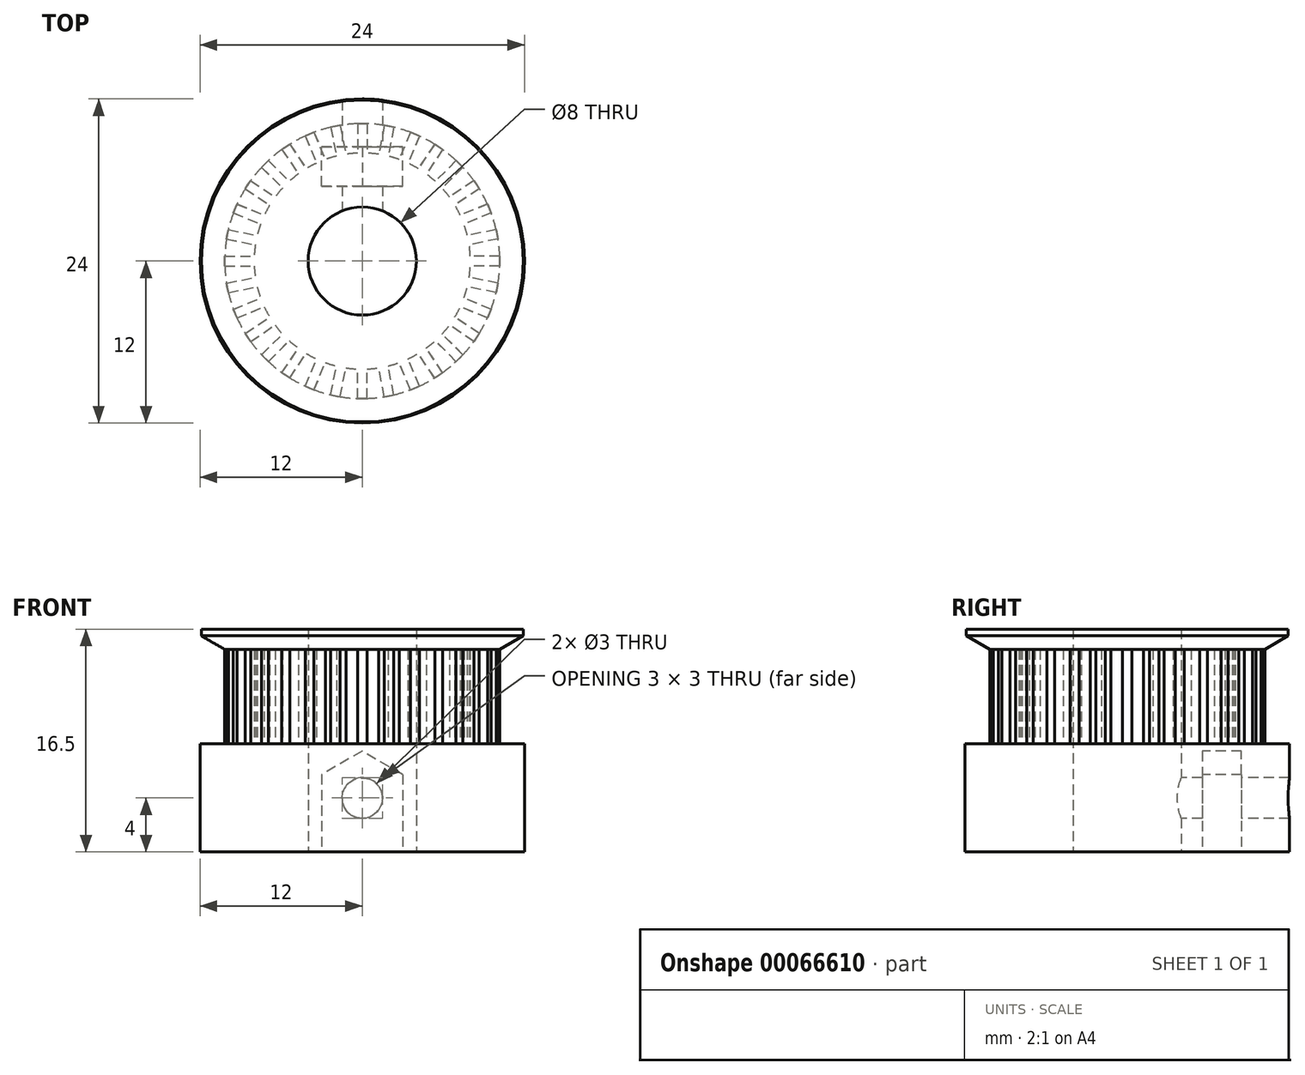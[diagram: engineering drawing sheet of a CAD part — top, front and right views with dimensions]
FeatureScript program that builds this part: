
annotation { "Feature Type Name" : "Feature", "Feature Type Description" : "" }
export const myFeature = defineFeature(function(context is Context, id is Id, definition is map)
    precondition{}
    {
        {
            var Q0;
            Q0=qCreatedBy(makeId("Top.planeOp"),FACE);
            var sketch = newSketch(context, id + "F0", { "sketchPlane" : qUnion([Q0])});
            skLineSegment(sketch, "E0", {"start": v(0, 0) * mm, "end": v(0, 9.87) * mm, "construction": true});
            skArc(sketch, "E1", {"start": v(-1.5, 2) * mm, "mid": v(0, -2.5) * mm, "end": v(1.5, 2) * mm, "construction": true});
            skLineSegment(sketch, "E2", {"start": v(0, 2) * mm, "end": v(-1.5, 2) * mm, "construction": true});
            skLineSegment(sketch, "E3.MirrorCS", {"start": v(0, 2) * mm, "end": v(1.5, 2) * mm, "construction": true});
            skArc(sketch, "E4.0", {"start": v(-1.57, 2.2) * mm, "mid": v(0, -2.7) * mm, "end": v(1.57, 2.2) * mm});
            skLineSegment(sketch, "E4.1", {"start": v(0, 2.2) * mm, "end": v(-1.57, 2.2) * mm});
            skLineSegment(sketch, "E4.2", {"start": v(0, 2.2) * mm, "end": v(1.57, 2.2) * mm});
            skCircle(sketch, "E5", {"center": v(0, 0) * mm, "radius": 12 * mm});
            skSolve(sketch);
        }
        {
            var Q0;
            Q0=makeQuery(id+"F0.imprint","IMPRINT",FACE,{"disambiguationData":[TD([[makeQuery(id+"F0.imprint","IMPRINT",EDGE,{"derivedFrom":sQuery(id+"F0.wireOp",EDGE,"E4.0")}),-1.0]])]});
            extrude(context, id + "F1", {"entities" : qUnion([Q0]), "depth" : 8 * mm});
        }
        {
            var Q0;
            Q0=makeQuery(id+"F1.opExtrude","CAP_FACE",FACE,{"disambiguationData":[OSD([sQuery(id+"F0.wireOp",EDGE,"E4.0"),sQuery(id+"F0.wireOp",EDGE,"E4.1"),sQuery(id+"F0.wireOp",EDGE,"E4.2"),sQuery(id+"F0.wireOp",EDGE,"E5")])],"isStart":true});
            var sketch = newSketch(context, id + "F2", { "sketchPlane" : qUnion([Q0])});
            skLineSegment(sketch, "E6.rect.bottom", {"start": v(-3, -5.55) * mm, "end": v(3, -5.55) * mm});
            skLineSegment(sketch, "E6.rect.top", {"start": v(-3, -8.45) * mm, "end": v(3, -8.45) * mm});
            skLineSegment(sketch, "E6.rect.left", {"start": v(-3, -5.55) * mm, "end": v(-3, -8.45) * mm});
            skLineSegment(sketch, "E6.rect.right", {"start": v(3, -5.55) * mm, "end": v(3, -8.45) * mm});
            skPoint(sketch, "E6.rect.middle", {"position": v(0, -7) * mm});
            skSolve(sketch);
        }
        {
            var Q0;
            Q0=makeQuery(id+"F2.imprint","IMPRINT",FACE,{"disambiguationData":[TD([[makeQuery(id+"F2.imprint","IMPRINT",EDGE,{"derivedFrom":sQuery(id+"F2.wireOp",EDGE,"E6.rect.bottom")}),-1.0]])]});
            extrude(context, id + "F3", {"entities" : qUnion([Q0]), "operationType" : NewBodyOperationType.REMOVE, "oppositeDirection" : true, "depth" : 4 * mm});
        }
        {
            var Q0;
            Q0=qCreatedBy(makeId("Front.planeOp"),FACE);
            var sketch = newSketch(context, id + "F4", { "sketchPlane" : qUnion([Q0])});
            skPoint(sketch, "E7", {"position": v(0, 4) * mm});
            skSolve(sketch);
        }
        {
            var Q0;
            Q0=sQuery(id+"F4.wireOp",VERTEX,"E7");
            var Q1;
            Q1=makeQuery(id+"F1.opExtrude","SWEPT_BODY",BODY,{"disambiguationData":[OSD([sQuery(id+"F0.wireOp",EDGE,"E4.0"),sQuery(id+"F0.wireOp",EDGE,"E4.1"),sQuery(id+"F0.wireOp",EDGE,"E4.2"),sQuery(id+"F0.wireOp",EDGE,"E5")])]});
            hole(context, id + "F5", {"style" : HoleStyle.SIMPLE, "holeDiameter" : 3 * mm, "endStyle" : HoleEndStyle.BLIND, "holeDepth" : 10 * mm, "locations" : qUnion([Q0]), "scope" : qUnion([Q1])});
        }
        {
            var Q0;
            Q0=makeQuery(id+"F3.boolean.opBoolean","COPY",FACE,{"derivedFrom":makeQuery(id+"F3.opExtrude","SWEPT_FACE",FACE,{"disambiguationData":[OSD([sQuery(id+"F2.wireOp",EDGE,"E6.rect.bottom")])]})});
            var sketch = newSketch(context, id + "F6", { "sketchPlane" : qUnion([Q0])});
            skCircle(sketch, "E8.cCircle", {"center": v(0, 4) * mm, "radius": 3 * mm, "construction": true});
            skLineSegment(sketch, "E8.0", {"start": v(3, 5.73) * mm, "end": v(3, 2.27) * mm});
            skLineSegment(sketch, "E8.1", {"start": v(3, 2.27) * mm, "end": v(0, 0.54) * mm});
            skLineSegment(sketch, "E8.2", {"start": v(0, 0.54) * mm, "end": v(-3, 2.27) * mm});
            skLineSegment(sketch, "E8.3", {"start": v(-3, 2.27) * mm, "end": v(-3, 5.73) * mm});
            skLineSegment(sketch, "E8.4", {"start": v(-3, 5.73) * mm, "end": v(0, 7.46) * mm});
            skLineSegment(sketch, "E8.5", {"start": v(0, 7.46) * mm, "end": v(3, 5.73) * mm});
            skPoint(sketch, "E8.0.midPoint", {"position": v(3, 4) * mm});
            skSolve(sketch);
        }
        {
            var Q0;
            Q0 = qSketchRegion(id + "F6", true);
            var Q1;
            Q1=makeQuery(id+"F3.boolean.opBoolean","COPY",FACE,{"derivedFrom":makeQuery(id+"F3.opExtrude","SWEPT_FACE",FACE,{"disambiguationData":[OSD([sQuery(id+"F2.wireOp",EDGE,"E6.rect.top")])]})});
            extrude(context, id + "F7", {"entities" : qUnion([Q0]), "operationType" : NewBodyOperationType.REMOVE, "endBound" : BoundingType.UP_TO_SURFACE, "endBoundEntityFace" : qUnion([Q1]), "depth" : 25 * mm});
        }
        {
            var Q0;
            Q0=makeQuery(id+"F1.opExtrude","CAP_FACE",FACE,{"disambiguationData":[OSD([sQuery(id+"F0.wireOp",EDGE,"E4.0"),sQuery(id+"F0.wireOp",EDGE,"E4.1"),sQuery(id+"F0.wireOp",EDGE,"E4.2"),sQuery(id+"F0.wireOp",EDGE,"E5")])],"isStart":false});
            var sketch = newSketch(context, id + "F8", { "sketchPlane" : qUnion([Q0])});
            skLineSegment(sketch, "E9.rect.bottom", {"start": v(0.35, -10.18) * mm, "end": v(-0.36, -10.18) * mm});
            skLineSegment(sketch, "E9.rect.top", {"start": v(0.35, -2.7) * mm, "end": v(-0.36, -2.7) * mm, "construction": true});
            skLineSegment(sketch, "E9.rect.left", {"start": v(0.35, -10.18) * mm, "end": v(0.35, -2.68) * mm});
            skLineSegment(sketch, "E9.rect.right", {"start": v(-0.36, -10.18) * mm, "end": v(-0.36, -2.68) * mm});
            skPoint(sketch, "E9.rect.middle", {"position": v(0, -6.44) * mm});
            skArc(sketch, "E10.0", {"start": v(-0.36, -2.68) * mm, "mid": v(0, -2.7) * mm, "end": v(0.35, -2.68) * mm});
            skPoint(sketch, "E11.orphan", {"position": v(-1.57, 2.2) * mm});
            skPoint(sketch, "E12.orphan", {"position": v(1.57, 2.2) * mm});
            skSolve(sketch);
        }
        {
            var Q0;
            Q0=makeQuery(id+"F8.imprint","IMPRINT",FACE,{"disambiguationData":[TD([[makeQuery(id+"F8.imprint","IMPRINT",EDGE,{"derivedFrom":sQuery(id+"F8.wireOp",EDGE,"E9.rect.bottom")}),-1.0]])]});
            var Q1;
            {var subQ0=sQuery(id+"F8.wireOp",EDGE,"E10.0");Q1=makeQuery(id+"F8.imprint","IMPRINT",FACE,{"disambiguationData":[TD([[makeQuery(id+"F8.imprint","IMPRINT",EDGE,{"derivedFrom":subQ0}),-1.0]])]});}
            extrude(context, id + "F9", {"entities" : qUnion([Q0, Q1]), "depth" : 7 * mm});
        }
        {
            var Q0;
            Q0=makeQuery(id+"F9.opExtrude","SWEPT_BODY",BODY,{"disambiguationData":[OSD([sQuery(id+"F8.wireOp",EDGE,"E9.rect.bottom"),sQuery(id+"F8.wireOp",EDGE,"E9.rect.left"),sQuery(id+"F8.wireOp",EDGE,"E9.rect.right"),sQuery(id+"F8.wireOp",EDGE,"E10.0")])]});
            var Q1;
            Q1=makeQuery(id+"F1.opExtrude","SWEPT_FACE",FACE,{"disambiguationData":[OSD([sQuery(id+"F0.wireOp",EDGE,"E5")])]});
            circularPattern(context, id + "F10", {"operationType" : NewBodyOperationType.ADD, "entities" : qUnion([Q0]), "axis" : qUnion([Q1]), "angle" : 360 * degree, "instanceCount" : 32, "equalSpace" : true});
        }
        {
            var Q0;
            {var subQ3=sQuery(id+"F0.wireOp",EDGE,"E5");Q0=makeQuery(id+"F10.boolean.opBoolean","SPLIT",FACE,{"disambiguationData":[TD([makeQuery(id+"F1.opExtrude","SWEPT_FACE",FACE,{"disambiguationData":[OSD([subQ3])]})])],"derivedFrom":makeQuery(id+"F1.opExtrude","CAP_FACE",FACE,{"disambiguationData":[OSD([sQuery(id+"F0.wireOp",EDGE,"E4.0"),sQuery(id+"F0.wireOp",EDGE,"E4.1"),sQuery(id+"F0.wireOp",EDGE,"E4.2"),subQ3])],"isStart":false})});}
            var sketch = newSketch(context, id + "F11", { "sketchPlane" : qUnion([Q0])});
            skArc(sketch, "E13.0", {"start": v(-1.57, 2.2) * mm, "mid": v(0, -2.7) * mm, "end": v(1.57, 2.2) * mm});
            skLineSegment(sketch, "E14.0", {"start": v(1.57, 2.2) * mm, "end": v(-1.57, 2.2) * mm});
            skCircle(sketch, "E15", {"center": v(0, 0) * mm, "radius": 8 * mm});
            skSolve(sketch);
        }
        {
            var Q0;
            Q0 = qSketchRegion(id + "F11", true);
            extrude(context, id + "F12", {"entities" : qUnion([Q0]), "operationType" : NewBodyOperationType.ADD, "depth" : 8.5 * mm});
        }
        {
            var Q0;
            Q0=qCreatedBy(makeId("Front.planeOp"),FACE);
            var sketch = newSketch(context, id + "F13", { "sketchPlane" : qUnion([Q0])});
            skLineSegment(sketch, "E16", {"start": v(0, 17.03) * mm, "end": v(0, 21.95) * mm, "construction": true});
            skLineSegment(sketch, "E17", {"start": v(-8, 15) * mm, "end": v(-8, 16.5) * mm});
            skLineSegment(sketch, "E18", {"start": v(-8, 15) * mm, "end": v(-10.18, 15) * mm});
            skLineSegment(sketch, "E19", {"start": v(-10.18, 15) * mm, "end": v(-11.9, 16) * mm});
            skLineSegment(sketch, "E20", {"start": v(-11.9, 16.5) * mm, "end": v(-8, 16.5) * mm});
            skLineSegment(sketch, "E21", {"start": v(-11.9, 16) * mm, "end": v(-11.9, 16.5) * mm});
            skPoint(sketch, "E22.orphan", {"position": v(-12.77, 16.5) * mm});
            skSolve(sketch);
        }
        {
            var Q0;
            Q0=makeQuery(id+"F13.imprint","IMPRINT",FACE,{"disambiguationData":[TD([[makeQuery(id+"F13.imprint","IMPRINT",EDGE,{"derivedFrom":sQuery(id+"F13.wireOp",EDGE,"E17")}),1.0]])]});
            var Q1;
            Q1=sQuery(id+"F13.wireOp",EDGE,"E16");
            revolve(context, id + "F14", {"operationType" : NewBodyOperationType.ADD, "entities" : qUnion([Q0]), "axis" : qUnion([Q1]), "revolveType" : RevolveType.FULL});
        }
        {
            var Q0;
            Q0=makeQuery(id+"F1.opExtrude","CAP_FACE",FACE,{"disambiguationData":[OSD([sQuery(id+"F0.wireOp",EDGE,"E4.0"),sQuery(id+"F0.wireOp",EDGE,"E4.1"),sQuery(id+"F0.wireOp",EDGE,"E4.2"),sQuery(id+"F0.wireOp",EDGE,"E5")])],"isStart":true});
            var sketch = newSketch(context, id + "F15", { "sketchPlane" : qUnion([Q0])});
            skCircle(sketch, "E23", {"center": v(0, 0) * mm, "radius": 4 * mm});
            skSolve(sketch);
        }
        {
            var Q0;
            Q0=makeQuery(id+"F15.imprint","IMPRINT",FACE,{"disambiguationData":[TD([[makeQuery(id+"F15.imprint","IMPRINT",EDGE,{"derivedFrom":sQuery(id+"F15.wireOp",EDGE,"E23")}),1.0]])]});
            extrude(context, id + "F16", {"entities" : qUnion([Q0]), "operationType" : NewBodyOperationType.REMOVE, "endBound" : BoundingType.THROUGH_ALL, "oppositeDirection" : true, "depth" : 25 * mm});
        }
    });
